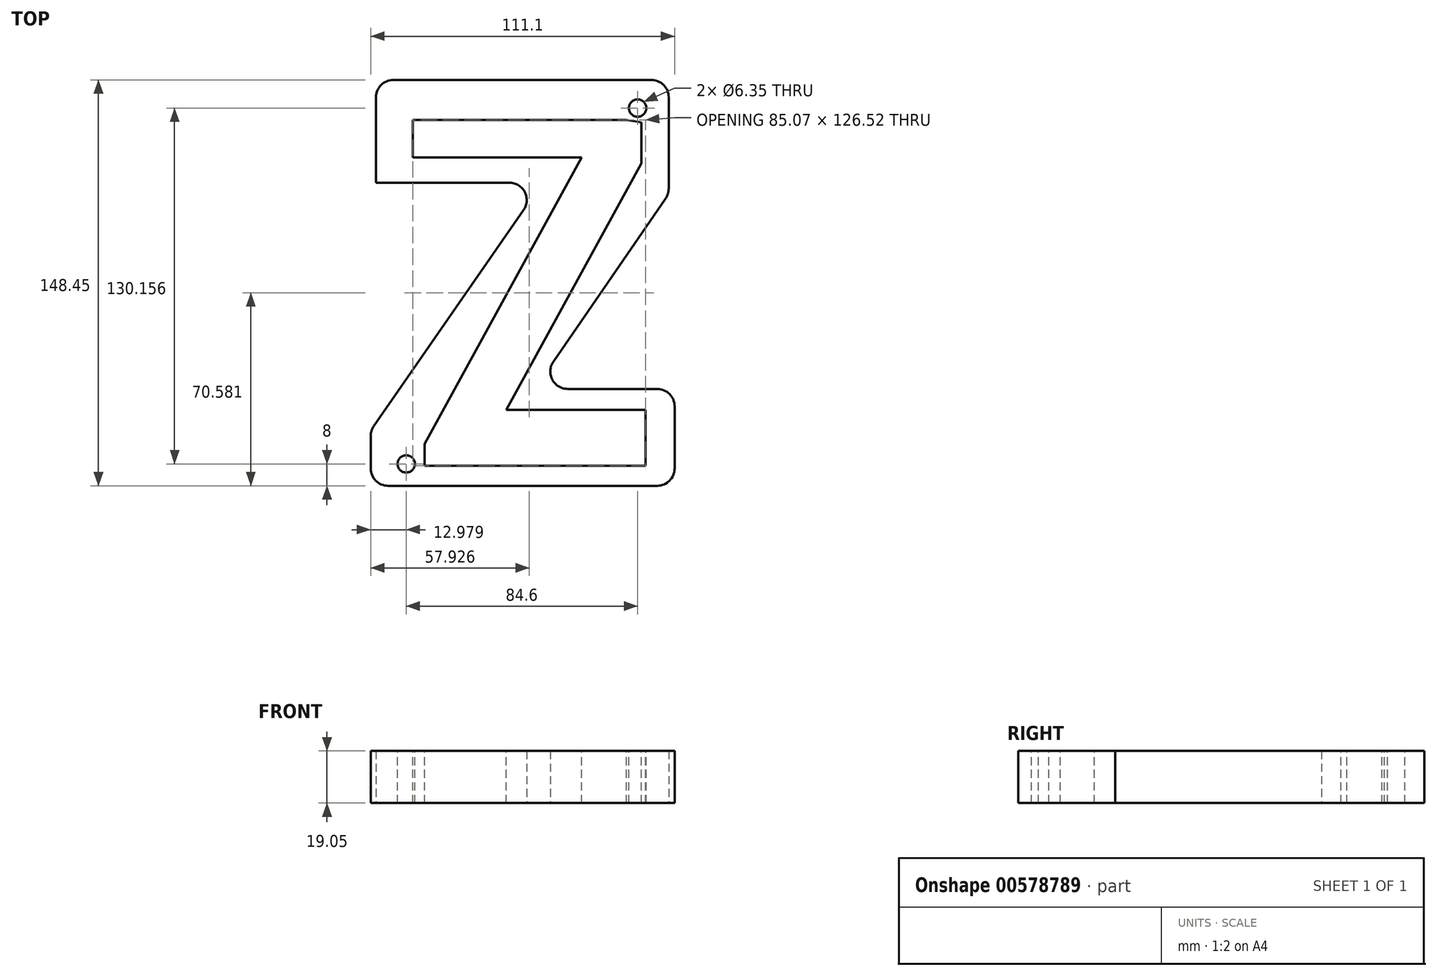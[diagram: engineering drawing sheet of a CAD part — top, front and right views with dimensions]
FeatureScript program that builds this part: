
annotation { "Feature Type Name" : "Feature", "Feature Type Description" : "" }
export const myFeature = defineFeature(function(context is Context, id is Id, definition is map)
    precondition{}
    {
        {
            var Q0;
            Q0=qCreatedBy(makeId("Top.planeOp"),FACE);
            var sketch = newSketch(context, id + "F0", { "sketchPlane" : qUnion([Q0])});
            skText(sketch, "E0", { "text": "Z", "fontName": "OpenSans-Bold.ttf"});
            skLineSegment(sketch, "E1", {"start": v(-54.55, 77.63) * mm, "end": v(-54.55, 38.1) * mm});
            skLineSegment(sketch, "E2", {"start": v(-54.55, 38.1) * mm, "end": v(-5.8, 38.1) * mm});
            skLineSegment(sketch, "E3", {"start": v(-0.58, 28.14) * mm, "end": v(-55.35, -50.87) * mm});
            skLineSegment(sketch, "E4", {"start": v(-56.48, -54.49) * mm, "end": v(-56.48, -66.4) * mm});
            skLineSegment(sketch, "E5", {"start": v(-50.13, -72.75) * mm, "end": v(48.27, -72.75) * mm});
            skLineSegment(sketch, "E6", {"start": v(54.62, -66.4) * mm, "end": v(54.62, -43.67) * mm});
            skLineSegment(sketch, "E7", {"start": v(48.27, -37.32) * mm, "end": v(15.52, -37.32) * mm});
            skLineSegment(sketch, "E8", {"start": v(10.29, -27.38) * mm, "end": v(51.33, 32.37) * mm});
            skLineSegment(sketch, "E9", {"start": v(52.45, 35.97) * mm, "end": v(52.45, 69.35) * mm});
            skLineSegment(sketch, "E10", {"start": v(46.1, 75.7) * mm, "end": v(-48.2, 75.7) * mm});
            skLineSegment(sketch, "E11", {"start": v(-54.55, 69.35) * mm, "end": v(-54.55, 38.1) * mm});
            skPoint(sketch, "E12.visualSharp", {"position": v(-54.55, 75.7) * mm});
            skArc(sketch, "E12.filletArc", {"start": v(-48.2, 75.7) * mm, "mid": v(-52.7, 73.84) * mm, "end": v(-54.55, 69.35) * mm});
            skPoint(sketch, "E13.visualSharp", {"position": v(6.33, 38.1) * mm});
            skArc(sketch, "E13.filletArc", {"start": v(-0.58, 28.14) * mm, "mid": v(-0.17, 34.7) * mm, "end": v(-5.8, 38.1) * mm});
            skPoint(sketch, "E14.visualSharp", {"position": v(-56.48, -52.5) * mm});
            skArc(sketch, "E14.filletArc", {"start": v(-55.35, -50.87) * mm, "mid": v(-56.2, -52.6) * mm, "end": v(-56.48, -54.49) * mm});
            skPoint(sketch, "E15.visualSharp", {"position": v(-56.48, -72.75) * mm});
            skArc(sketch, "E15.filletArc", {"start": v(-56.48, -66.4) * mm, "mid": v(-54.62, -70.89) * mm, "end": v(-50.13, -72.75) * mm});
            skPoint(sketch, "E16.visualSharp", {"position": v(54.62, -72.75) * mm});
            skArc(sketch, "E16.filletArc", {"start": v(48.27, -72.75) * mm, "mid": v(52.76, -70.89) * mm, "end": v(54.62, -66.4) * mm});
            skPoint(sketch, "E17.visualSharp", {"position": v(54.62, -37.32) * mm});
            skArc(sketch, "E17.filletArc", {"start": v(54.62, -43.67) * mm, "mid": v(52.76, -39.18) * mm, "end": v(48.27, -37.32) * mm});
            skPoint(sketch, "E18.visualSharp", {"position": v(3.46, -37.32) * mm});
            skArc(sketch, "E18.filletArc", {"start": v(10.29, -27.38) * mm, "mid": v(9.9, -33.93) * mm, "end": v(15.52, -37.32) * mm});
            skPoint(sketch, "E19.visualSharp", {"position": v(52.45, 34) * mm});
            skArc(sketch, "E19.filletArc", {"start": v(51.33, 32.37) * mm, "mid": v(52.16, 34.09) * mm, "end": v(52.45, 35.97) * mm});
            skPoint(sketch, "E20.visualSharp", {"position": v(52.45, 75.7) * mm});
            skArc(sketch, "E20.filletArc", {"start": v(52.45, 69.35) * mm, "mid": v(50.59, 73.84) * mm, "end": v(46.1, 75.7) * mm});
            skLineSegment(sketch, "E21", {"start": v(-54.55, 75.7) * mm, "end": v(-54.55, 38.1) * mm});
            const initialGuessF0  = {"E0": [-0.06154, -0.07275, 1, 0, 0.15038]};
            skSetInitialGuess(sketch, initialGuessF0);
            skSolve(sketch);
        }
        {
            var Q0;
            {var subQ5=sQuery(id+"F0.wireOp",EDGE,"E2");Q0=makeQuery(id+"F0.imprint","IMPRINT",FACE,{"disambiguationData":[TD([[makeQuery(id+"F0.imprint","IMPRINT",EDGE,{"derivedFrom":subQ5}),1.0]])]});}
            var Q1;
            {var subQ6=sQuery(id+"F0.wireOp",EDGE,"E0.sketch_text.stroke-8");Q1=makeQuery(id+"F0.imprint","IMPRINT",FACE,{"disambiguationData":[TD([[makeQuery(id+"F0.imprint","IMPRINT",EDGE,{"derivedFrom":subQ6}),-1.0]])]});}
            var Q2;
            {var subQ0=sQuery(id+"F0.wireOp",EDGE,"E0.sketch_text.stroke-8");Q2=makeQuery(id+"F0.imprint","IMPRINT",FACE,{"disambiguationData":[TD([[makeQuery(id+"F0.imprint","IMPRINT",EDGE,{"derivedFrom":subQ0}),1.0]])]});}
            extrude(context, id + "F1", {"entities" : qUnion([Q0, Q1, Q2]), "depth" : 19.05 * mm, "offsetDistance" : 25.4 * mm});
        }
        {
            var Q0;
            Q0=makeQuery(id+"F1.opExtrude","CAP_FACE",FACE,{"disambiguationData":[OSD([sQuery(id+"F0.wireOp",EDGE,"E2"),sQuery(id+"F0.wireOp",EDGE,"E3"),sQuery(id+"F0.wireOp",EDGE,"E4"),sQuery(id+"F0.wireOp",EDGE,"E5"),sQuery(id+"F0.wireOp",EDGE,"E6"),sQuery(id+"F0.wireOp",EDGE,"E7"),sQuery(id+"F0.wireOp",EDGE,"E8"),sQuery(id+"F0.wireOp",EDGE,"E9"),sQuery(id+"F0.wireOp",EDGE,"E10"),sQuery(id+"F0.wireOp",EDGE,"E12.filletArc"),sQuery(id+"F0.wireOp",EDGE,"E13.filletArc"),sQuery(id+"F0.wireOp",EDGE,"E14.filletArc"),sQuery(id+"F0.wireOp",EDGE,"E15.filletArc"),sQuery(id+"F0.wireOp",EDGE,"E16.filletArc"),sQuery(id+"F0.wireOp",EDGE,"E17.filletArc"),sQuery(id+"F0.wireOp",EDGE,"E18.filletArc"),sQuery(id+"F0.wireOp",EDGE,"E19.filletArc"),sQuery(id+"F0.wireOp",EDGE,"E20.filletArc"),sQuery(id+"F0.wireOp",EDGE,"E21")])],"isStart":false});
            var sketch = newSketch(context, id + "F2", { "sketchPlane" : qUnion([Q0])});
            skLineSegment(sketch, "E22", {"start": v(-54.62, -70.89) * mm, "end": v(-43.5, -64.75) * mm});
            skLineSegment(sketch, "E23", {"start": v(50.59, 73.84) * mm, "end": v(41.1, 65.4) * mm});
            skCircle(sketch, "E24", {"center": v(41.1, 65.4) * mm, "radius": 3.17 * mm});
            skCircle(sketch, "E25", {"center": v(-43.5, -64.75) * mm, "radius": 3.18 * mm});
            skSolve(sketch);
        }
        {
            var Q0;
            Q0=makeQuery(id+"F2.imprint","IMPRINT",FACE,{"disambiguationData":[TD([[makeQuery(id+"F2.imprint","IMPRINT",EDGE,{"derivedFrom":sQuery(id+"F2.wireOp",EDGE,"E24")}),1.0]])]});
            var Q1;
            Q1=makeQuery(id+"F2.imprint","IMPRINT",FACE,{"disambiguationData":[TD([[makeQuery(id+"F2.imprint","IMPRINT",EDGE,{"derivedFrom":sQuery(id+"F2.wireOp",EDGE,"E25")}),1.0]])]});
            extrude(context, id + "F3", {"entities" : qUnion([Q0, Q1]), "operationType" : NewBodyOperationType.REMOVE, "oppositeDirection" : true, "depth" : 25.4 * mm, "offsetDistance" : 25.4 * mm});
        }
        {
            var Q0;
            Q0=makeQuery(id+"F1.opExtrude","CAP_FACE",FACE,{"disambiguationData":[OSD([sQuery(id+"F0.wireOp",EDGE,"E2"),sQuery(id+"F0.wireOp",EDGE,"E3"),sQuery(id+"F0.wireOp",EDGE,"E4"),sQuery(id+"F0.wireOp",EDGE,"E5"),sQuery(id+"F0.wireOp",EDGE,"E6"),sQuery(id+"F0.wireOp",EDGE,"E7"),sQuery(id+"F0.wireOp",EDGE,"E8"),sQuery(id+"F0.wireOp",EDGE,"E9"),sQuery(id+"F0.wireOp",EDGE,"E10"),sQuery(id+"F0.wireOp",EDGE,"E12.filletArc"),sQuery(id+"F0.wireOp",EDGE,"E13.filletArc"),sQuery(id+"F0.wireOp",EDGE,"E14.filletArc"),sQuery(id+"F0.wireOp",EDGE,"E15.filletArc"),sQuery(id+"F0.wireOp",EDGE,"E16.filletArc"),sQuery(id+"F0.wireOp",EDGE,"E17.filletArc"),sQuery(id+"F0.wireOp",EDGE,"E18.filletArc"),sQuery(id+"F0.wireOp",EDGE,"E19.filletArc"),sQuery(id+"F0.wireOp",EDGE,"E20.filletArc"),sQuery(id+"F0.wireOp",EDGE,"E21")])],"isStart":false});
            var sketch = newSketch(context, id + "F4", { "sketchPlane" : qUnion([Q0])});
            skLineSegment(sketch, "E26", {"start": v(37, 61.1) * mm, "end": v(-41.09, 61.1) * mm});
            skLineSegment(sketch, "E27", {"start": v(-41.09, 61.1) * mm, "end": v(-41.09, 47.36) * mm});
            skLineSegment(sketch, "E28", {"start": v(-41.09, 47.36) * mm, "end": v(20.6, 47.36) * mm});
            skLineSegment(sketch, "E29", {"start": v(20.6, 47.36) * mm, "end": v(-36.75, -57.48) * mm});
            skLineSegment(sketch, "E30", {"start": v(-36.75, -57.48) * mm, "end": v(-36.75, -65.43) * mm});
            skLineSegment(sketch, "E31", {"start": v(-36.75, -65.43) * mm, "end": v(43.98, -65.43) * mm});
            skLineSegment(sketch, "E32", {"start": v(43.98, -65.43) * mm, "end": v(43.98, -44.95) * mm});
            skLineSegment(sketch, "E33", {"start": v(43.98, -44.95) * mm, "end": v(-6.87, -44.95) * mm});
            skLineSegment(sketch, "E34", {"start": v(-6.87, -44.95) * mm, "end": v(42.47, 45.22) * mm});
            skLineSegment(sketch, "E35", {"start": v(42.47, 45.22) * mm, "end": v(42.47, 60.13) * mm});
            skLineSegment(sketch, "E36", {"start": v(42.47, 60.13) * mm, "end": v(37, 61.1) * mm});
            skSolve(sketch);
        }
        {
            var Q0;
            Q0 = qSketchRegion(id + "F4", true);
            extrude(context, id + "F5", {"entities" : qUnion([Q0]), "operationType" : NewBodyOperationType.REMOVE, "endBound" : BoundingType.THROUGH_ALL, "oppositeDirection" : true, "depth" : 25.4 * mm, "offsetDistance" : 25.4 * mm});
        }
    });
